# Revit family: EUB
name_source: partatom
category: Mechanical Equipment
units: mm (PartAtom-declared; Revit-internal decimal feet)

## family parameters
Always vertical = Yes
Cut with Voids When Loaded = No
Part Type = Normal
Room Calculation Point = No
Round Connector Dimension = Use Diameter
Shared = No
Work Plane-Based = No

## types (8) — shared parameters
0 = 0"
1" = 1"
1' = 12"
1.5 = 1 1/2"
2" = 2"
2' = 24"
4" = 4"
E = 3"
E-.125" = 2 7/8"
Manufacturer = Loren Cook Company
Model = EUB
ONE EIGTH = 1/8"
Type Comments = Upblast Exhaust Ventilator Extruded Aluminum Propeller Roof Mounted/Belt Drive
URL = www.lorencook.com

## per-type parameters (varying)
| type | (A/2)-4" | (A/2)-4.125" | (T_SQ/2)+.125" | -(A/2) | -(C/2) | A | A/2 | B | B/2 | C | C-B | C-B-3" | C_/2 | D | E+C-B-2" | RO | RO/2 | T_SQ | T_SQ/2 | T_SQ/6 |
| 24_EUB | 11 1/2" | 11 3/8" | 18 1/8" | -15 1/2" | -9 9/16" | 31" | 15 1/2" | 19 1/8" | 9 9/16" | 47 3/4" | 28 5/8" | 25 5/8" | 23 7/8" | 4" | 29 5/8" | 31 1/2" | 15 3/4" | 36" | 18" | 6" |
| 30_EUB | 14 1/2" | 14 3/8" | 21 1/8" | -18 1/2" | -11 13/16" | 37" | 18 1/2" | 23 5/8" | 11 13/16" | 52 3/8" | 28 3/4" | 25 3/4" | 26 3/16" | 3 7/8" | 29 3/4" | 37 1/2" | 18 3/4" | 42" | 21" | 7" |
| 36_EUB | 17 1/2" | 17 3/8" | 24 1/8" | -21 1/2" | -12 13/16" | 43" | 21 1/2" | 25 5/8" | 12 13/16" | 60 7/8" | 35 1/4" | 32 1/4" | 30 7/16" | 4" | 36 1/4" | 43 1/2" | 21 3/4" | 48" | 24" | 8" |
| 42_EUB | 20 1/2" | 20 3/8" | 27 1/8" | -24 1/2" | -13 15/16" | 49" | 24 1/2" | 27 7/8" | 13 15/16" | 63 5/8" | 35 3/4" | 32 3/4" | 31 13/16" | 4" | 36 3/4" | 49 1/2" | 24 3/4" | 54" | 27" | 9" |
| 48_EUB | 23 1/2" | 23 3/8" | 30 1/8" | -27 1/2" | -15 5/8" | 55" | 27 1/2" | 31 1/4" | 15 5/8" | 67" | 35 3/4" | 32 3/4" | 33 1/2" | 4" | 36 3/4" | 55 1/2" | 27 3/4" | 60" | 30" | 10" |
| 54_EUB | 26 1/2" | 26 3/8" | 33 1/8" | -30 1/2" | -17 5/8" | 61" | 30 1/2" | 35 1/4" | 17 5/8" | 77" | 41 3/4" | 38 3/4" | 38 1/2" | 4" | 42 3/4" | 61 1/2" | 30 3/4" | 66" | 33" | 11" |
| 60_EUB | 29 1/2" | 29 3/8" | 36 1/8" | -33 1/2" | -18 1/4" | 67" | 33 1/2" | 36 1/2" | 18 1/4" | 78 1/4" | 41 3/4" | 38 3/4" | 39 1/8" | 4" | 42 3/4" | 67 1/2" | 33 3/4" | 72" | 36" | 12" |
| 72_EUB | 35 1/2" | 35 3/8" | 42 1/8" | -39 1/2" | -22" | 79" | 39 1/2" | 44" | 22" | 92 3/4" | 48 3/4" | 45 3/4" | 46 3/8" | 3 1/2" | 49 3/4" | 79 1/2" | 39 3/4" | 84" | 42" | 14" |

## geometry (parser evidence)
native form markers: Sweep x2
no freeform markers — native parametric forms only
